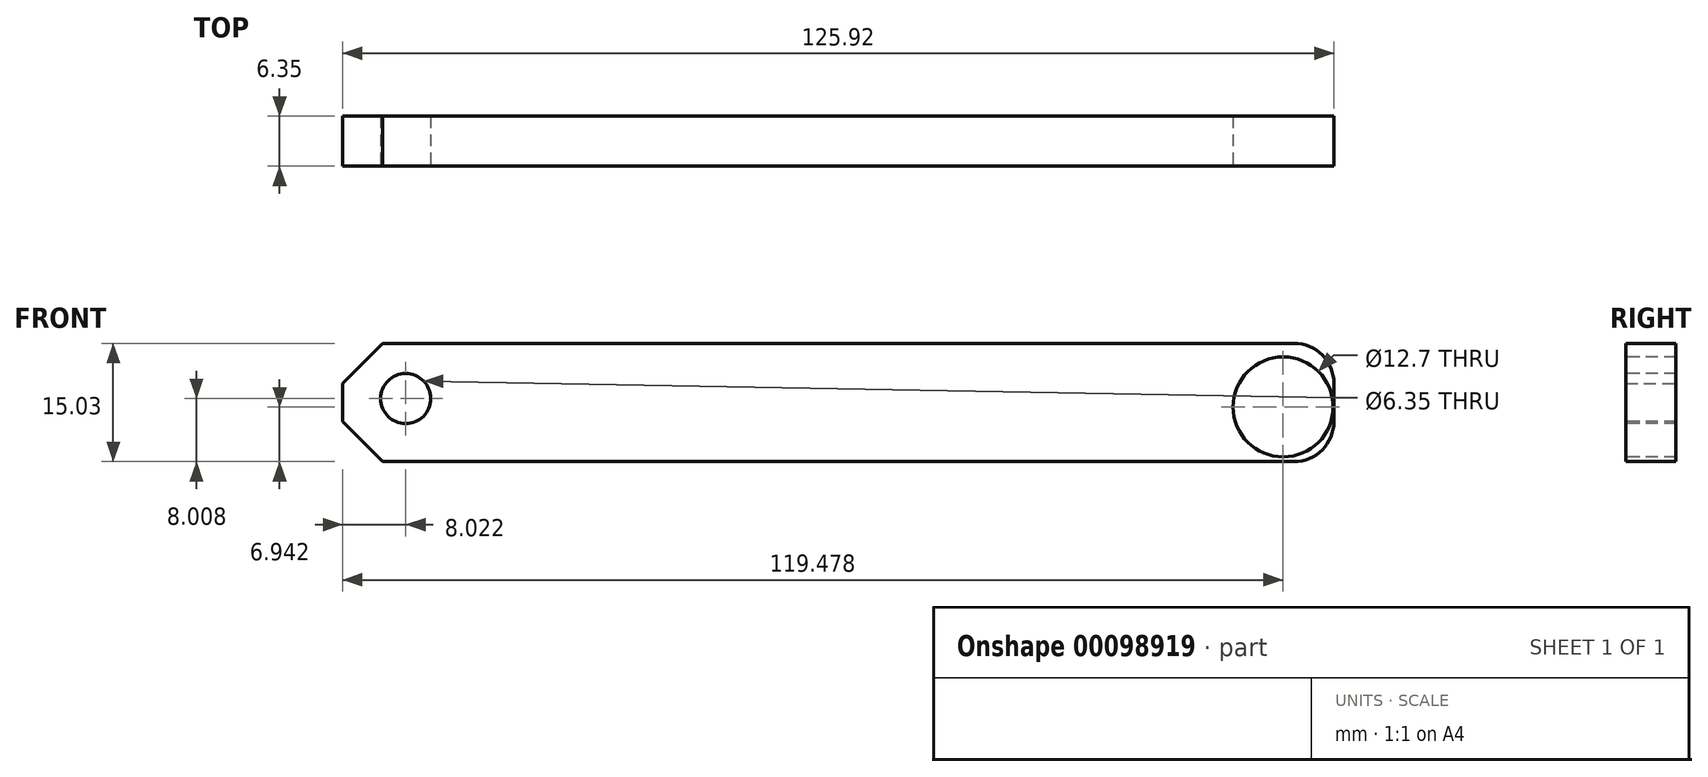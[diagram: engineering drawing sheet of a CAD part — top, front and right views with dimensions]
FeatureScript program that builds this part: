
annotation { "Feature Type Name" : "Feature", "Feature Type Description" : "" }
export const myFeature = defineFeature(function(context is Context, id is Id, definition is map)
    precondition{}
    {
        {
            var Q0;
            Q0=qCreatedBy(makeId("Front.planeOp"),FACE);
            var sketch = newSketch(context, id + "F0", { "sketchPlane" : qUnion([Q0])});
            skLineSegment(sketch, "E0.bottom", {"start": v(-58.47, 24.84) * mm, "end": v(67.45, 24.84) * mm});
            skLineSegment(sketch, "E0.top", {"start": v(-58.47, 9.8) * mm, "end": v(67.45, 9.8) * mm});
            skLineSegment(sketch, "E0.left", {"start": v(-58.47, 24.84) * mm, "end": v(-58.47, 9.8) * mm});
            skLineSegment(sketch, "E0.right", {"start": v(67.45, 24.84) * mm, "end": v(67.45, 9.8) * mm});
            skSolve(sketch);
        }
        {
            var Q0;
            Q0=makeQuery(id+"F0.imprint","IMPRINT",FACE,{"disambiguationData":[TD([[makeQuery(id+"F0.imprint","IMPRINT",EDGE,{"derivedFrom":sQuery(id+"F0.wireOp",EDGE,"E0.bottom")}),-1.0]])]});
            extrude(context, id + "F1", {"entities" : qUnion([Q0]), "depth" : 6.35 * mm});
        }
        {
            var Q0;
            Q0=makeQuery(id+"F1.opExtrude","SWEPT_EDGE",EDGE,{"disambiguationData":[OSD([sQuery(id+"F0.wireOp",EDGE,"E0.bottom"),sQuery(id+"F0.wireOp",EDGE,"E0.right")])]});
            var Q1;
            Q1=makeQuery(id+"F1.opExtrude","SWEPT_EDGE",EDGE,{"disambiguationData":[OSD([sQuery(id+"F0.wireOp",EDGE,"E0.top"),sQuery(id+"F0.wireOp",EDGE,"E0.right")])]});
            fillet(context, id + "F2", {"entities" : qUnion([Q0, Q1]), "radius" : 5.08 * mm, "tangentPropagation" : true, "allowEdgeOverflow" : false});
        }
        {
            var Q0;
            Q0=makeQuery(id+"F1.opExtrude","SWEPT_EDGE",EDGE,{"disambiguationData":[OSD([sQuery(id+"F0.wireOp",EDGE,"E0.bottom"),sQuery(id+"F0.wireOp",EDGE,"E0.left")])]});
            var Q1;
            Q1=makeQuery(id+"F1.opExtrude","SWEPT_EDGE",EDGE,{"disambiguationData":[OSD([sQuery(id+"F0.wireOp",EDGE,"E0.top"),sQuery(id+"F0.wireOp",EDGE,"E0.left")])]});
            chamfer(context, id + "F3", {"entities" : qUnion([Q0, Q1]), "width" : 5.08 * mm, "tangentPropagation" : true});
        }
        {
            var Q0;
            Q0=makeQuery(id+"F1.opExtrude","CAP_FACE",FACE,{"disambiguationData":[OSD([sQuery(id+"F0.wireOp",EDGE,"E0.bottom"),sQuery(id+"F0.wireOp",EDGE,"E0.top"),sQuery(id+"F0.wireOp",EDGE,"E0.left"),sQuery(id+"F0.wireOp",EDGE,"E0.right")])],"isStart":false});
            var sketch = newSketch(context, id + "F4", { "sketchPlane" : qUnion([Q0])});
            skPoint(sketch, "E1", {"position": v(61, 16.75) * mm});
            skSolve(sketch);
        }
        {
            var Q0;
            Q0=sQuery(id+"F4.wireOp",VERTEX,"E1");
            var Q1;
            Q1=makeQuery(id+"F1.opExtrude","SWEPT_BODY",BODY,{"disambiguationData":[OSD([sQuery(id+"F0.wireOp",EDGE,"E0.bottom"),sQuery(id+"F0.wireOp",EDGE,"E0.top"),sQuery(id+"F0.wireOp",EDGE,"E0.left"),sQuery(id+"F0.wireOp",EDGE,"E0.right")])]});
            hole(context, id + "F5", {"style" : HoleStyle.SIMPLE, "endStyle" : HoleEndStyle.THROUGH, "holeDiameter" : 12.7 * mm, "locations" : qUnion([Q0]), "scope" : qUnion([Q1]), "isTappedThrough" : true});
        }
        {
            var Q0;
            Q0=makeQuery(id+"F1.opExtrude","CAP_FACE",FACE,{"disambiguationData":[OSD([sQuery(id+"F0.wireOp",EDGE,"E0.bottom"),sQuery(id+"F0.wireOp",EDGE,"E0.top"),sQuery(id+"F0.wireOp",EDGE,"E0.left"),sQuery(id+"F0.wireOp",EDGE,"E0.right")])],"isStart":false});
            var sketch = newSketch(context, id + "F6", { "sketchPlane" : qUnion([Q0])});
            skPoint(sketch, "E2", {"position": v(-50.45, 17.82) * mm});
            skSolve(sketch);
        }
        {
            var Q0;
            Q0=sQuery(id+"F6.wireOp",VERTEX,"E2");
            var Q1;
            Q1=makeQuery(id+"F1.opExtrude","SWEPT_BODY",BODY,{"disambiguationData":[OSD([sQuery(id+"F0.wireOp",EDGE,"E0.bottom"),sQuery(id+"F0.wireOp",EDGE,"E0.top"),sQuery(id+"F0.wireOp",EDGE,"E0.left"),sQuery(id+"F0.wireOp",EDGE,"E0.right")])]});
            hole(context, id + "F7", {"style" : HoleStyle.SIMPLE, "endStyle" : HoleEndStyle.THROUGH, "holeDiameter" : 6.35 * mm, "locations" : qUnion([Q0]), "scope" : qUnion([Q1]), "isTappedThrough" : true});
        }
    });
